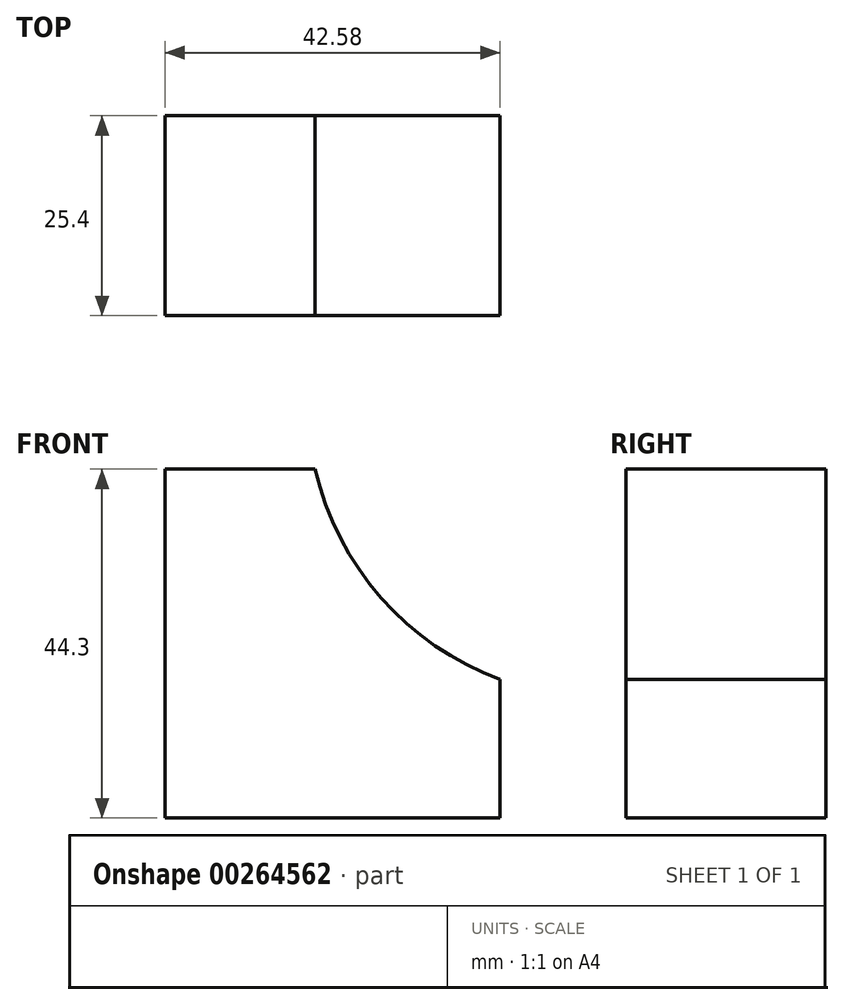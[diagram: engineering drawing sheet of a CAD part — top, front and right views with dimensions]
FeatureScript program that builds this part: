
annotation { "Feature Type Name" : "Feature", "Feature Type Description" : "" }
export const myFeature = defineFeature(function(context is Context, id is Id, definition is map)
    precondition{}
    {
        {
            var Q0;
            Q0=qCreatedBy(makeId("Front.planeOp"),FACE);
            var sketch = newSketch(context, id + "F0", { "sketchPlane" : qUnion([Q0])});
            skLineSegment(sketch, "E0", {"start": v(0, 0) * mm, "end": v(-42.58, 0) * mm});
            skLineSegment(sketch, "E1", {"start": v(-42.58, 0) * mm, "end": v(-42.58, 44.3) * mm});
            skLineSegment(sketch, "E2", {"start": v(-42.58, 44.3) * mm, "end": v(-23.49, 44.3) * mm});
            skLineSegment(sketch, "E3", {"start": v(0, 17.57) * mm, "end": v(0, 0) * mm});
            skArc(sketch, "E4", {"start": v(-23.49, 44.3) * mm, "mid": v(-15.13, 27.96) * mm, "end": v(0, 17.57) * mm});
            skSolve(sketch);
        }
        {
            var Q0;
            Q0 = qSketchRegion(id + "F0", true);
            extrude(context, id + "F1", {"entities" : qUnion([Q0]), "depth" : 25.4 * mm});
        }
    });
